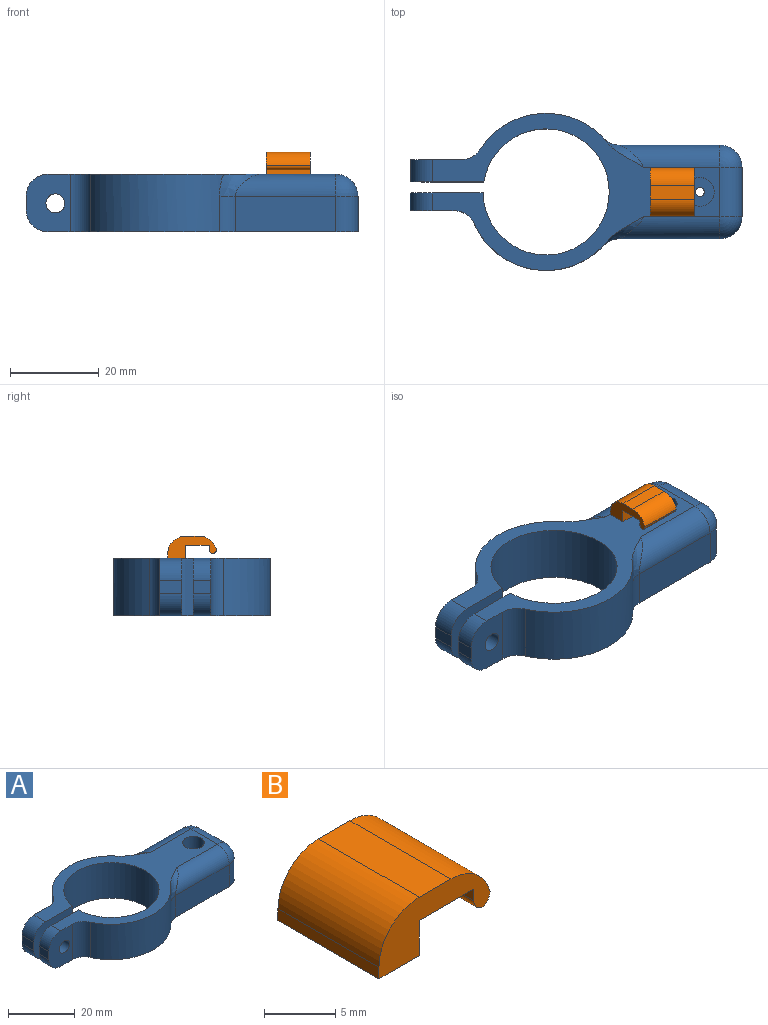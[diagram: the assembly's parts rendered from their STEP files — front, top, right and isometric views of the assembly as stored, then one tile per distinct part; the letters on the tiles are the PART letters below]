
ASSEMBLY  parts=2 mates=1
PART A: 48 faces, bbox 77.3x37.8x20.3 mm
  f0: plane 70x35.5mm, normal (0,0,-1), area 906.3mm2, adj f1,f2,f3,f5,f6,f7,f17,f20
  f1: cylinder r=17.75mm len=28.79mm, axis (0,0,-1), area 422.9mm2, adj f0,f4,f36,f42,f43
  f2: cylinder r=17.75mm len=30.06mm, axis (0,0,-1), area 457.8mm2, adj f0,f4,f39,f44,f45
  f3: cylinder r=14.25mm len=28.5mm, axis (0,0,-1), area 1131.3mm2, adj f0,f4,f5,f6
  f4: plane 67.3x37.8mm, normal (0,0,1), area 653.6mm2, adj f1,f2,f3,f5,f6,f7,f17,f30
  f5: plane 16.54x13mm, normal (0,-1,0), area 189.7mm2, adj f0,f3,f4,f13,f15,f37,f38
  f6: plane 16.5x13mm, normal (0,1,0), area 189.3mm2, adj f0,f3,f4,f18,f19,f40,f41
  f7: plane 13x11.44mm, normal (0,1,0), area 82.6mm2, adj f0,f4,f8,f9,f10,f11,f12,f13
  f8: plane 4x3.4mm, normal (-0.87,0,0.5), area 15.7mm2, adj f7,f9,f14,f16
  f9: plane 4.62x3.4mm, normal (0,0,1), area 15.7mm2, adj f7,f8,f10,f16
  f10: plane 4x3.4mm, normal (0.87,0,0.5), area 15.7mm2, adj f7,f9,f11,f16
  f11: plane 4x3.4mm, normal (0.87,0,-0.5), area 15.7mm2, adj f7,f10,f12,f16
  f12: plane 4.62x3.4mm, normal (0,0,-1), area 15.7mm2, adj f7,f11,f14,f16
  f13: plane 5x3mm, normal (-1,0,0), area 15mm2, adj f5,f7,f37,f38
  f14: plane 4x3.4mm, normal (-0.87,0,-0.5), area 15.7mm2, adj f7,f8,f12,f16
  f15: cylinder r=2.15mm len=4.3mm, axis (0,-1,0), area 21.6mm2, adj f5,f16
  f16: plane 9.24x8mm, normal (0,1,0), area 40.9mm2, adj f8,f9,f10,f11,f12,f14,f15
  f17: plane 13x9.96mm, normal (0,-1,0), area 104.2mm2, adj f0,f4,f18,f19,f39,f40,f41
  f18: plane 4x3mm, normal (-1,0,0), area 12mm2, adj f6,f17,f40,f41
  f19: cylinder r=2.15mm len=4.3mm, axis (0,1,0), area 54mm2, adj f6,f17
  f20: plane 22.68x8mm, normal (0,1,0), area 181.4mm2, adj f0,f33,f35,f42
  f21: plane 22.68x8mm, normal (0,-1,0), area 181.4mm2, adj f0,f29,f30,f44
  f22: plane 11.17x8mm, normal (1,0,0), area 89.3mm2, adj f0,f29,f32,f35
  f23: plane 7x5mm, normal (-1,0,0), area 35mm2, adj f0,f24,f26,f27
  f24: plane 13x5mm, normal (0,1,0), area 65mm2, adj f0,f23,f25,f27
  f25: plane 7x5mm, normal (1,0,0), area 35mm2, adj f0,f24,f26,f27
  f26: plane 13x5mm, normal (0,-1,0), area 65mm2, adj f0,f23,f25,f27
  f27: plane 13x7mm, normal (0,0,-1), area 87.9mm2, adj f23,f24,f25,f26,f28
  f28: cylinder r=1mm len=2mm, axis (0,0,-1), area 12.6mm2, adj f27,f46
  f29: cylinder r=5mm len=8mm, axis (0,0,1), area 62.8mm2, adj f0,f21,f22,f31
  f30: cylinder r=5mm len=22.68mm, axis (1,0,0), area 156.6mm2, adj f4,f21,f31,f45
  f31: sphere r=5mm, area 39.3mm2, adj f29,f30,f32
  f32: cylinder r=5mm len=11.17mm, axis (0,1,0), area 87.7mm2, adj f4,f22,f31,f34
  f33: cylinder r=5mm len=22.68mm, axis (-1,0,0), area 156.6mm2, adj f4,f20,f34,f43
  f34: sphere r=5mm, area 39.3mm2, adj f32,f33,f35
  f35: cylinder r=5mm len=8mm, axis (0,0,-1), area 62.8mm2, adj f0,f20,f22,f34
  f36: cylinder r=5mm len=13mm, axis (0,0,-1), area 65.1mm2, adj f0,f1,f4,f7
  f37: cylinder r=5mm len=5mm, axis (0,-1,0), area 39.3mm2, adj f4,f5,f7,f13
  f38: cylinder r=5mm len=5mm, axis (0,1,0), area 39.3mm2, adj f0,f5,f7,f13
  f39: cylinder r=5mm len=13mm, axis (0,0,-1), area 74.9mm2, adj f0,f2,f4,f17
  f40: cylinder r=5mm len=5mm, axis (0,-1,0), area 31.4mm2, adj f4,f6,f17,f18
  f41: cylinder r=5mm len=5mm, axis (0,1,0), area 31.4mm2, adj f0,f6,f17,f18
  f42: cylinder r=5mm len=8mm, axis (0,0,-1), area 32.6mm2, adj f0,f1,f20,f43
  f43: bspline ~10.49x9.44mm, area 39.1mm2, adj f1,f4,f33,f42
  f44: cylinder r=5mm len=8mm, axis (0,0,-1), area 32.6mm2, adj f0,f2,f21,f45
  f45: bspline ~10.49x9.44mm, area 39.1mm2, adj f2,f4,f30,f44
  f46: plane 6.5x6.5mm, normal (0,0,1), area 30mm2, adj f28,f47
  f47: cylinder r=3.25mm len=6.5mm, axis (0,0,-1), area 122.5mm2, adj f4,f46
PART B: 12 faces, bbox 11x10x5 mm
  f0: plane 10x5.4mm, normal (0,0,-1), area 54mm2, adj f1,f3,f4,f7
  f1: plane 11x5mm, normal (0,1,0), area 30.3mm2, adj f0,f2,f4,f5,f6,f7,f8,f9
  f2: plane 10x1mm, normal (-1,0,0), area 10mm2, adj f1,f3,f6,f11
  f3: plane 11x5mm, normal (0,-1,0), area 30.3mm2, adj f0,f2,f4,f5,f6,f7,f8,f9
  f4: plane 10x3mm, normal (1,0,0), area 30mm2, adj f0,f1,f3,f6
  f5: plane 10x3.13mm, normal (0,0,1), area 31.3mm2, adj f1,f3,f10,f11
  f6: plane 10x4mm, normal (0,0,-1), area 40mm2, adj f1,f2,f3,f4
  f7: plane 10x1mm, normal (-1,0,0), area 10mm2, adj f0,f1,f3,f9
  f8: cylinder r=1mm len=10mm, axis (0,1,0), area 13.7mm2, adj f1,f3,f9,f10
  f9: cylinder r=1mm len=10mm, axis (0,-1,0), area 13.7mm2, adj f1,f3,f7,f8
  f10: cylinder r=4mm len=10mm, axis (0,1,0), area 52.7mm2, adj f1,f3,f5,f8
  f11: cylinder r=4mm len=10mm, axis (0,1,0), area 62.8mm2, adj f1,f2,f3,f5
PLACE A t=(-8.89,1.76,-1.5)mm
PLACE B rot(axis=(0,0,-1),90deg) t=(24.61,7.25,11.5)mm
MATE planar B.f6 <-> A.f4  axis (0,0,-1) through (19.61,7.25,11.5)mm
